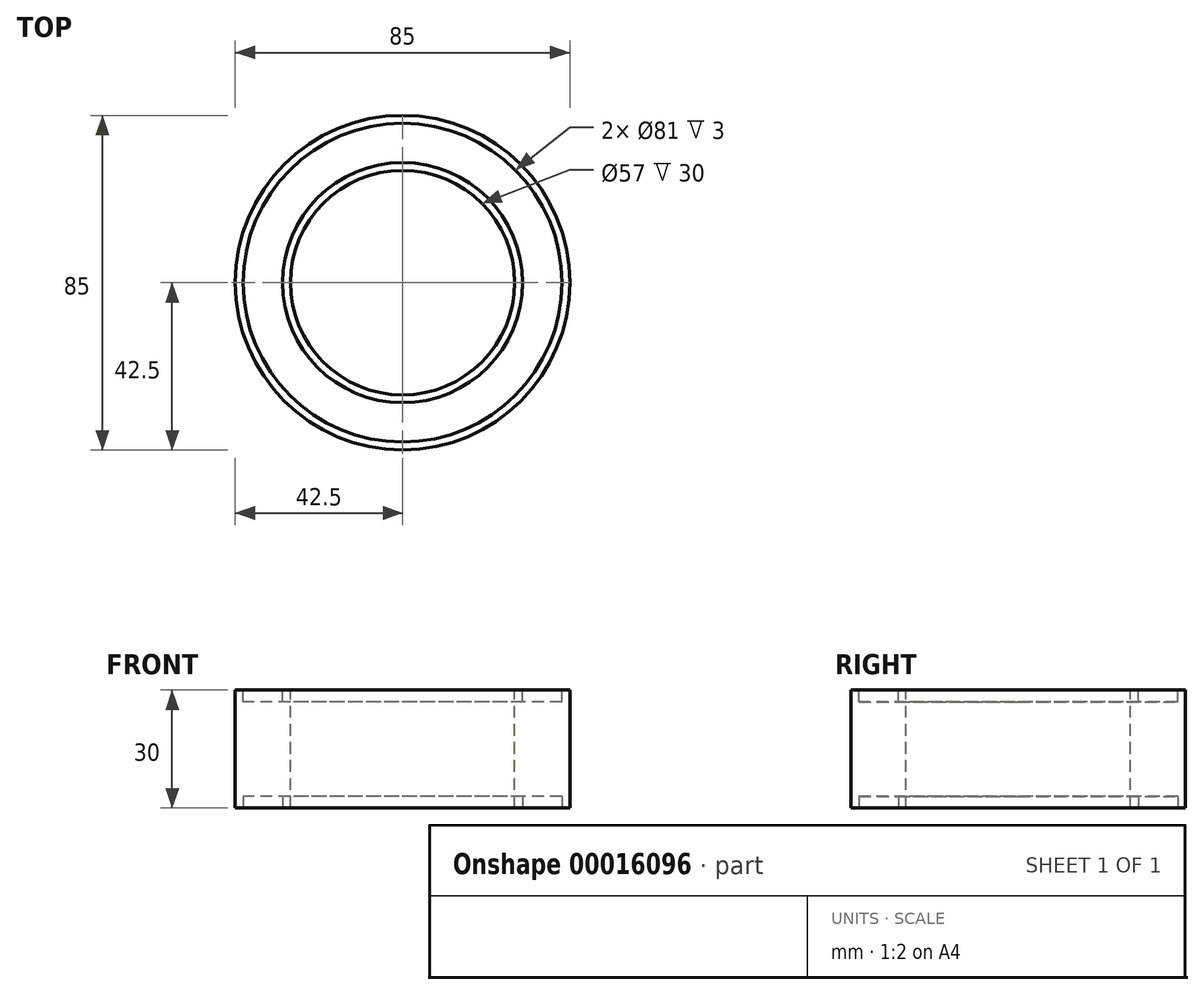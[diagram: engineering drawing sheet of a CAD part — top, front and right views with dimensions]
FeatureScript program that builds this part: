
annotation { "Feature Type Name" : "Feature", "Feature Type Description" : "" }
export const myFeature = defineFeature(function(context is Context, id is Id, definition is map)
    precondition{}
    {
        {
            var Q0;
            Q0=qCreatedBy(makeId("Top.planeOp"),FACE);
            var sketch = newSketch(context, id + "F0", { "sketchPlane" : qUnion([Q0])});
            skCircle(sketch, "E0", {"center": v(0, 0) * mm, "radius": 42.5 * mm});
            skSolve(sketch);
        }
        {
            var Q0;
            Q0=makeQuery(id+"F0.imprint","IMPRINT",FACE,{"disambiguationData":[TD([[makeQuery(id+"F0.imprint","IMPRINT",EDGE,{"derivedFrom":sQuery(id+"F0.wireOp",EDGE,"E0")}),1.0]])]});
            extrude(context, id + "F1", {"entities" : qUnion([Q0]), "depth" : 15 * mm});
        }
        {
            var Q0;
            Q0=makeQuery(id+"F1.opExtrude","CAP_FACE",FACE,{"disambiguationData":[OSD([sQuery(id+"F0.wireOp",EDGE,"E0")])],"isStart":false});
            var sketch = newSketch(context, id + "F2", { "sketchPlane" : qUnion([Q0])});
            skCircle(sketch, "E1", {"center": v(0, 0) * mm, "radius": 40.5 * mm});
            skCircle(sketch, "E2", {"center": v(0, 0) * mm, "radius": 30.5 * mm});
            skSolve(sketch);
        }
        {
            var Q0;
            Q0 = qSketchRegion(id + "F2", true);
            extrude(context, id + "F3", {"entities" : qUnion([Q0]), "operationType" : NewBodyOperationType.REMOVE, "oppositeDirection" : true, "depth" : 3 * mm});
        }
        {
            var Q0;
            Q0=makeQuery(id+"F3.boolean.opBoolean","SPLIT",FACE,{"disambiguationData":[TD([makeQuery(id+"F3.opExtrude","SWEPT_FACE",FACE,{"disambiguationData":[OSD([sQuery(id+"F2.wireOp",EDGE,"E2")])]})])],"derivedFrom":makeQuery(id+"F1.opExtrude","CAP_FACE",FACE,{"disambiguationData":[OSD([sQuery(id+"F0.wireOp",EDGE,"E0")])],"isStart":false})});
            var sketch = newSketch(context, id + "F4", { "sketchPlane" : qUnion([Q0])});
            skSolve(sketch);
        }
        {
            var Q0;
            Q0=makeQuery(id+"F4.imprint","IMPRINT",FACE,{"disambiguationData":[TD([[makeQuery(id+"F4.imprint","IMPRINT",EDGE,{"derivedFrom":makeQuery(id+"F3.boolean.opBoolean","COPY",EDGE,{"derivedFrom":makeQuery(id+"F3.opExtrude","CAP_EDGE",EDGE,{"disambiguationData":[OSD([sQuery(id+"F2.wireOp",EDGE,"E2")])],"isStart":true})})}),1.0]])]});
            var sketch = newSketch(context, id + "F5", { "sketchPlane" : qUnion([Q0])});
            skCircle(sketch, "E3", {"center": v(0, 0) * mm, "radius": 28.5 * mm});
            skSolve(sketch);
        }
        {
            var Q0;
            Q0 = qSketchRegion(id + "F5", true);
            extrude(context, id + "F6", {"entities" : qUnion([Q0]), "operationType" : NewBodyOperationType.REMOVE, "endBound" : BoundingType.THROUGH_ALL, "oppositeDirection" : true, "depth" : 25 * mm});
        }
        {
            var Q0;
            Q0=makeQuery(id+"F1.opExtrude","SWEPT_BODY",BODY,{"disambiguationData":[OSD([sQuery(id+"F0.wireOp",EDGE,"E0")])]});
            var Q1;
            Q1=qCreatedBy(makeId("Top.planeOp"),FACE);
            mirror(context, id + "F7", {"operationType" : NewBodyOperationType.ADD, "entities" : qUnion([Q0]), "mirrorPlane" : qUnion([Q1])});
        }
    });
